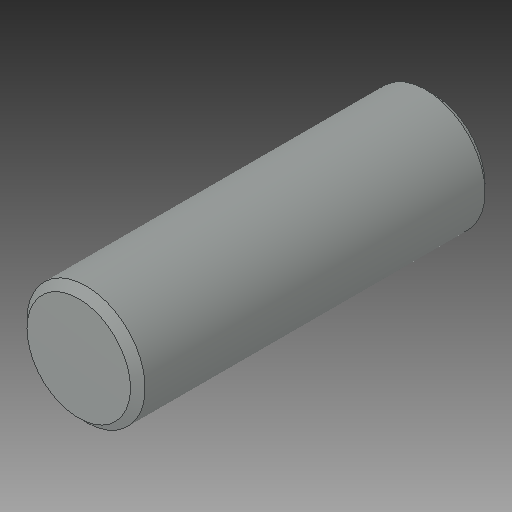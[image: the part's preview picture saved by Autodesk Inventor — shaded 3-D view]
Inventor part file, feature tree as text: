
AUTODESK INVENTOR PART (.ipt)
format: ipt  version: 2018 (Build 220112000, 112)  size: 98,816 bytes
history: native  units: in
note: dims shown in document units (in); Inventor stores cm internally (conversion verified against a paired STEP export)
features: chamfer x1
ambient origin geometry x8: Origin, YZ Plane, XZ Plane, XY Plane, X Axis, Y Axis, Z Axis, Center Point
bodies: Solid1 (feature_tree)
feature tree (1):
  chamfer  "Chamfer1"  [1 undecoded]
note: 1 required parameter value undecoded (feature->parameter linkage not recoverable at this tier; creation-order binding heuristic only, values carry confidence <= 0.55)
